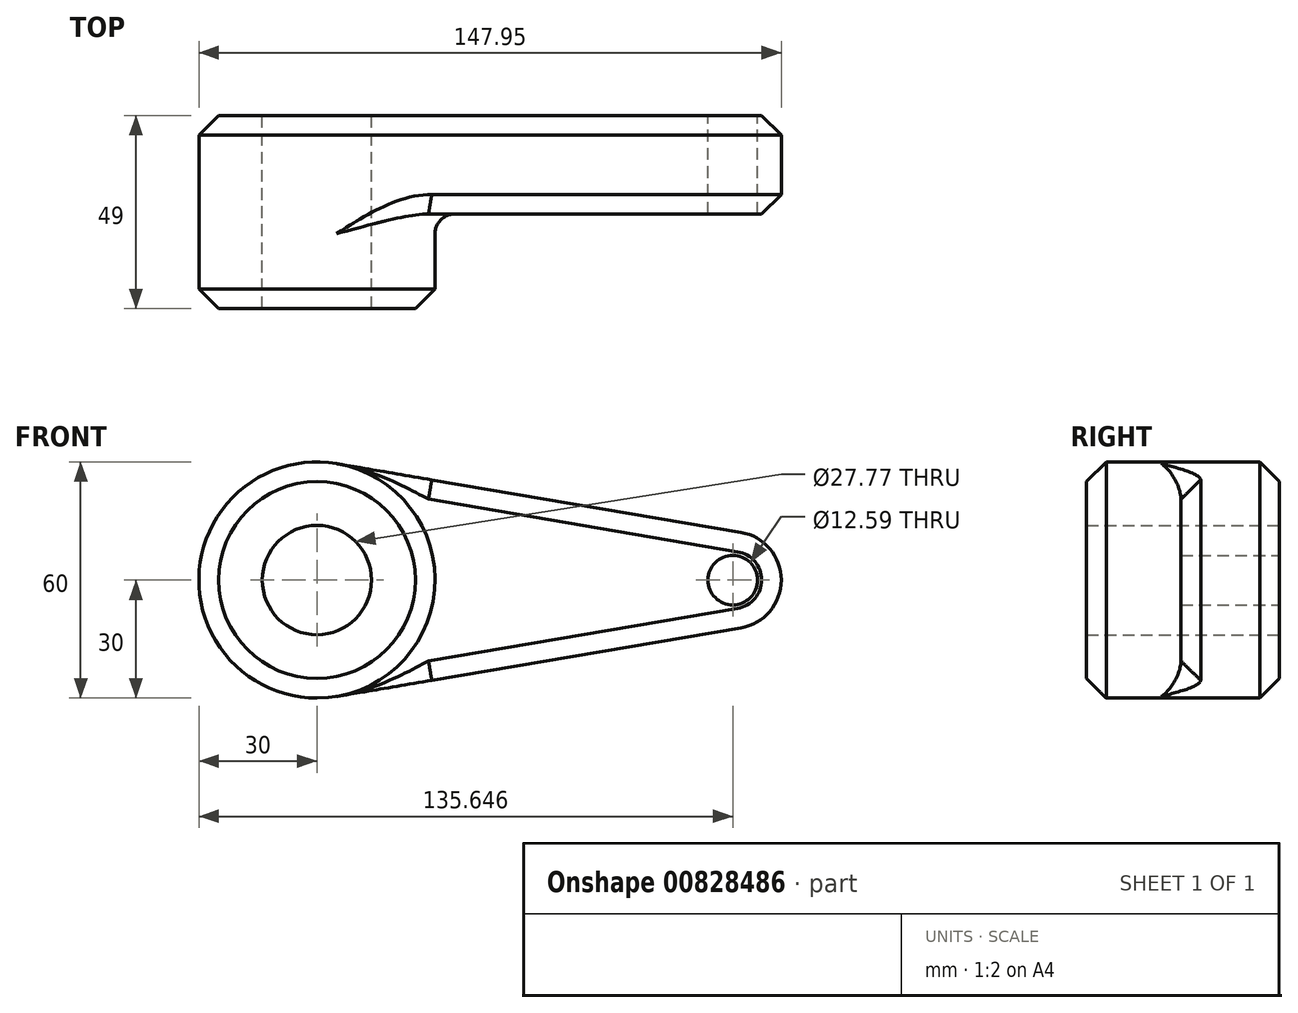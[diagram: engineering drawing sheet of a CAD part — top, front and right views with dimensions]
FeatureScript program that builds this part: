
annotation { "Feature Type Name" : "Feature", "Feature Type Description" : "" }
export const myFeature = defineFeature(function(context is Context, id is Id, definition is map)
    precondition{}
    {
        {
            var Q0;
            Q0=qCreatedBy(makeId("Front.planeOp"),FACE);
            var sketch = newSketch(context, id + "F0", { "sketchPlane" : qUnion([Q0])});
            skCircle(sketch, "E0", {"center": v(0, 0) * mm, "radius": 30 * mm});
            skCircle(sketch, "E1", {"center": v(105.65, 0) * mm, "radius": 12.3 * mm});
            skLineSegment(sketch, "E2", {"start": v(5.02, 29.58) * mm, "end": v(107.7, 12.13) * mm});
            skLineSegment(sketch, "E3", {"start": v(5.02, -29.58) * mm, "end": v(107.7, -12.13) * mm});
            skCircle(sketch, "E4", {"center": v(0, 0) * mm, "radius": 13.89 * mm});
            skCircle(sketch, "E5", {"center": v(105.65, 0) * mm, "radius": 6.3 * mm});
            skSolve(sketch);
        }
        {
            var Q0;
            Q0=makeQuery(id+"F0.imprint","IMPRINT",FACE,{"disambiguationData":[TD([[makeQuery(id+"F0.imprint","IMPRINT",EDGE,{"derivedFrom":sQuery(id+"F0.wireOp",EDGE,"E4")}),-1.0]])]});
            var Q1;
            {var subQ0=sQuery(id+"F0.wireOp",EDGE,"E2");Q1=makeQuery(id+"F0.imprint","IMPRINT",FACE,{"disambiguationData":[TD([[makeQuery(id+"F0.imprint","IMPRINT",EDGE,{"derivedFrom":subQ0}),-1.0]])]});}
            var Q2;
            Q2=makeQuery(id+"F0.imprint","IMPRINT",FACE,{"disambiguationData":[TD([[makeQuery(id+"F0.imprint","IMPRINT",EDGE,{"derivedFrom":sQuery(id+"F0.wireOp",EDGE,"E5")}),-1.0]])]});
            extrude(context, id + "F1", {"entities" : qUnion([Q0, Q1, Q2]), "depth" : 25 * mm, "offsetDistance" : 25 * mm});
        }
        {
            var Q0;
            Q0=makeQuery(id+"F0.imprint","IMPRINT",FACE,{"disambiguationData":[TD([[makeQuery(id+"F0.imprint","IMPRINT",EDGE,{"derivedFrom":sQuery(id+"F0.wireOp",EDGE,"E4")}),-1.0]])]});
            extrude(context, id + "F2", {"entities" : qUnion([Q0]), "operationType" : NewBodyOperationType.ADD, "depth" : 49 * mm, "offsetDistance" : 25 * mm});
        }
        {
            var Q0;
            {var subQ0=sQuery(id+"F0.wireOp",EDGE,"E0");Q0=makeQuery(id+"F2.boolean.opBoolean","INTERSECT",EDGE,{"derivedFrom":[makeQuery(id+"F1.opExtrude","CAP_FACE",FACE,{"disambiguationData":[OSD([subQ0,sQuery(id+"F0.wireOp",EDGE,"E1"),sQuery(id+"F0.wireOp",EDGE,"E2"),sQuery(id+"F0.wireOp",EDGE,"E3"),sQuery(id+"F0.wireOp",EDGE,"E4"),sQuery(id+"F0.wireOp",EDGE,"E5")])],"isStart":false}),makeQuery(id+"F2.opExtrude","SWEPT_FACE",FACE,{"disambiguationData":[OSD([subQ0])]})]});}
            fillet(context, id + "F3", {"entities" : qUnion([Q0]), "radius" : 5 * mm, "tangentPropagation" : true, "allowEdgeOverflow" : false});
        }
        {
            var Q0;
            Q0=makeQuery(id+"F1.opExtrude","CAP_EDGE",EDGE,{"disambiguationData":[OSD([sQuery(id+"F0.wireOp",EDGE,"E3")])],"isStart":true});
            var Q1;
            Q1=makeQuery(id+"F2.opExtrude","CAP_EDGE",EDGE,{"disambiguationData":[OSD([sQuery(id+"F0.wireOp",EDGE,"E0")])],"isStart":false});
            var Q2;
            Q2=makeQuery(id+"F1.opExtrude","CAP_EDGE",EDGE,{"disambiguationData":[OSD([sQuery(id+"F0.wireOp",EDGE,"E2")])],"isStart":false});
            chamfer(context, id + "F4", {"entities" : qUnion([Q0, Q1, Q2]), "width" : 5 * mm, "tangentPropagation" : true});
        }
    });
